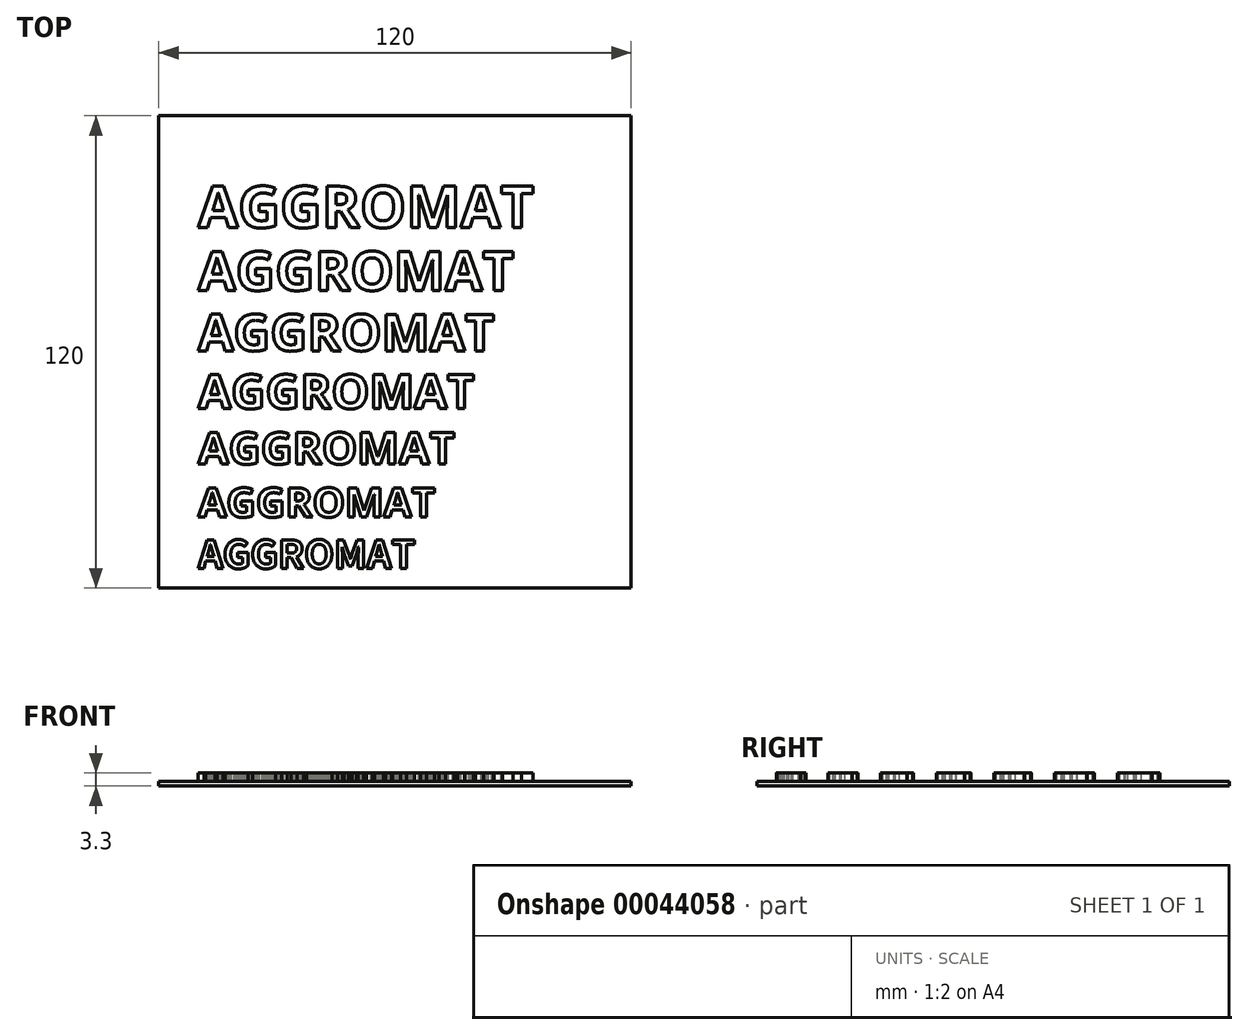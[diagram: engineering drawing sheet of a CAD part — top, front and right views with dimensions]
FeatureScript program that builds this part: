
annotation { "Feature Type Name" : "Feature", "Feature Type Description" : "" }
export const myFeature = defineFeature(function(context is Context, id is Id, definition is map)
    precondition{}
    {
        {
            var Q0;
            Q0=qCreatedBy(makeId("Top.planeOp"),FACE);
            var sketch = newSketch(context, id + "F0", { "sketchPlane" : qUnion([Q0])});
            skLineSegment(sketch, "E0.rect.bottom", {"start": v(60, -60) * mm, "end": v(-60, -60) * mm});
            skLineSegment(sketch, "E0.rect.top", {"start": v(60, 60) * mm, "end": v(-60, 60) * mm});
            skLineSegment(sketch, "E0.rect.left", {"start": v(60, -60) * mm, "end": v(60, 60) * mm});
            skLineSegment(sketch, "E0.rect.right", {"start": v(-60, -60) * mm, "end": v(-60, 60) * mm});
            skPoint(sketch, "E0.rect.middle", {"position": v(0, 0) * mm});
            skSolve(sketch);
        }
        {
            var Q0;
            Q0=makeQuery(id+"F0.imprint","IMPRINT",FACE,{"disambiguationData":[TD([[makeQuery(id+"F0.imprint","IMPRINT",EDGE,{"derivedFrom":sQuery(id+"F0.wireOp",EDGE,"E0.rect.bottom")}),-1.0]])]});
            extrude(context, id + "F1", {"entities" : qUnion([Q0]), "depth" : 1.2 * mm});
        }
        {
            var Q0;
            Q0=makeQuery(id+"F1.opExtrude","CAP_FACE",FACE,{"disambiguationData":[OSD([sQuery(id+"F0.wireOp",EDGE,"E0.rect.bottom"),sQuery(id+"F0.wireOp",EDGE,"E0.rect.top"),sQuery(id+"F0.wireOp",EDGE,"E0.rect.left"),sQuery(id+"F0.wireOp",EDGE,"E0.rect.right")])],"isStart":false});
            var sketch = newSketch(context, id + "F2", { "sketchPlane" : qUnion([Q0])});
            skText(sketch, "E1", { "text": "AGGROMAT", "fontName": "NotoSansCJKsc-Bold.otf"});
            skText(sketch, "E2", { "text": "AGGROMAT", "fontName": "OpenSans-Bold.ttf"});
            skText(sketch, "E3", { "text": "AGGROMAT", "fontName": "OpenSans-Bold.ttf"});
            skText(sketch, "E4", { "text": "AGGROMAT", "fontName": "OpenSans-Bold.ttf"});
            skText(sketch, "E5", { "text": "AGGROMAT", "fontName": "OpenSans-Bold.ttf"});
            skText(sketch, "E6", { "text": "AGGROMAT", "fontName": "OpenSans-Bold.ttf"});
            skText(sketch, "E7", { "text": "AGGROMAT", "fontName": "OpenSans-Bold.ttf"});
            const initialGuessF2  = {"E1": [-0.05, -0.055, 1, 0, 0.00704], "E2": [-0.05, -0.04196, 1, 0, 0.00747], "E3": [-0.05, -0.0285, 1, 0, 0.00809], "E4": [-0.05, -0.0144, 1, 0, 0.00871], "E5": [-0.05, 0.0003, 1, 0, 0.00933], "E6": [-0.05, 0.01564, 1, 0, 0.00995], "E7": [-0.05, 0.0316, 1, 0, 0.01058]};
            skSetInitialGuess(sketch, initialGuessF2);
            skSolve(sketch);
        }
        {
            var Q0;
            Q0=qSketchRegion(id+"F2",true);
            extrude(context, id + "F3", {"entities" : qUnion([Q0]), "operationType" : NewBodyOperationType.ADD, "depth" : 2.1 * mm});
        }
    });
